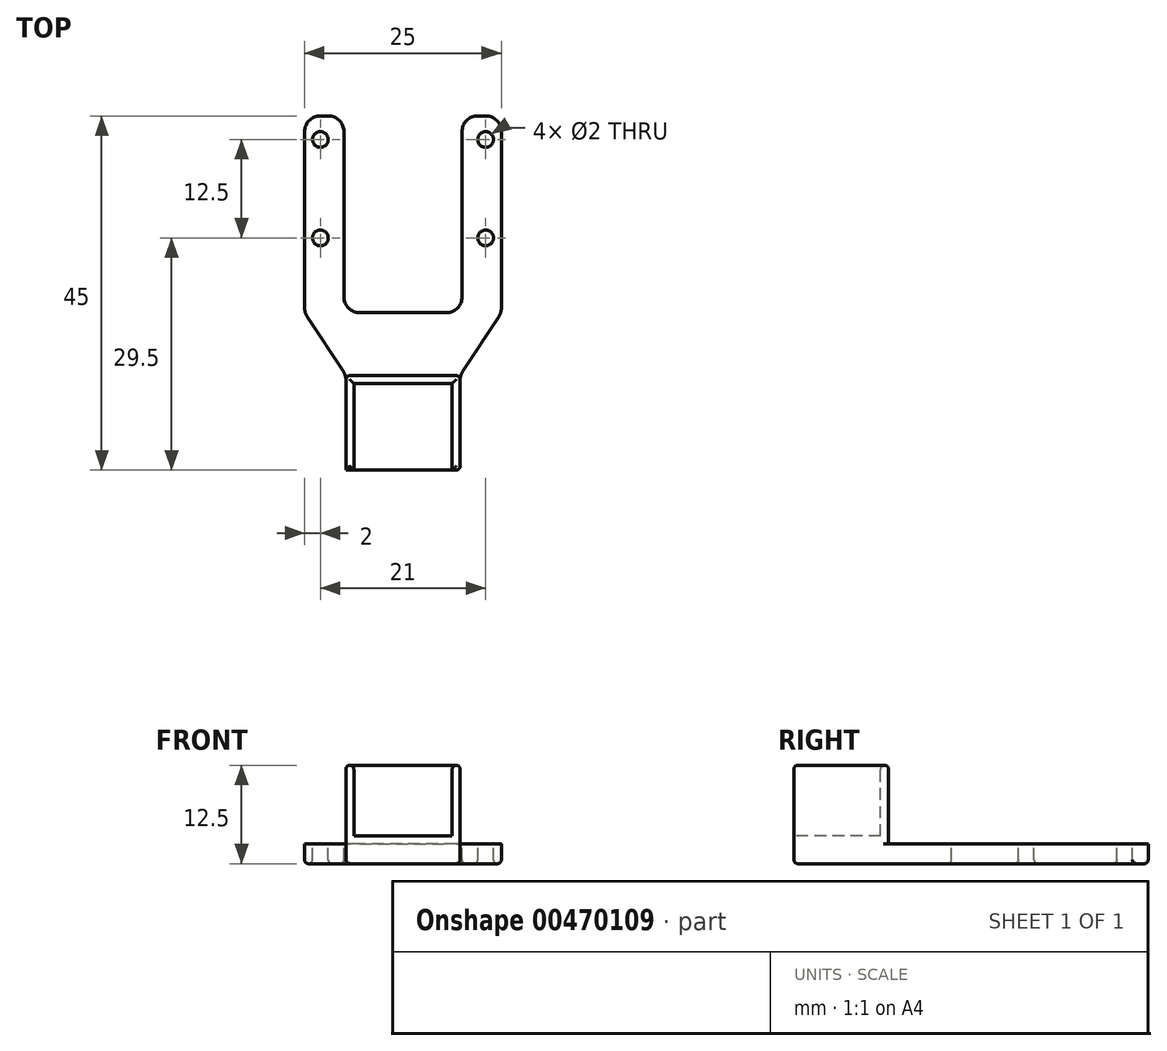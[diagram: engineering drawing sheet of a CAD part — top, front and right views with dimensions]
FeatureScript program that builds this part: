
annotation { "Feature Type Name" : "Feature", "Feature Type Description" : "" }
export const myFeature = defineFeature(function(context is Context, id is Id, definition is map)
    precondition{}
    {
        {
            var Q0;
            Q0=qCreatedBy(makeId("Top.planeOp"),FACE);
            var sketch = newSketch(context, id + "F0", { "sketchPlane" : qUnion([Q0])});
            skLineSegment(sketch, "E0", {"start": v(0, 0) * mm, "end": v(14.5, 0) * mm});
            skLineSegment(sketch, "E1", {"start": v(14.5, 0) * mm, "end": v(14.5, 12) * mm});
            skLineSegment(sketch, "E2", {"start": v(14.5, 12) * mm, "end": v(0, 12) * mm});
            skLineSegment(sketch, "E3", {"start": v(0, 12) * mm, "end": v(0, 0) * mm});
            skSolve(sketch);
        }
        {
            var Q0;
            Q0=makeQuery(id+"F0.imprint","IMPRINT",FACE,{"disambiguationData":[TD([[makeQuery(id+"F0.imprint","IMPRINT",EDGE,{"derivedFrom":sQuery(id+"F0.wireOp",EDGE,"E0")}),1.0]])]});
            extrude(context, id + "F1", {"entities" : qUnion([Q0]), "depth" : 10 * mm});
        }
        {
            var Q0;
            Q0=makeQuery(id+"F1.opExtrude","CAP_FACE",FACE,{"disambiguationData":[OSD([sQuery(id+"F0.wireOp",EDGE,"E0"),sQuery(id+"F0.wireOp",EDGE,"E1"),sQuery(id+"F0.wireOp",EDGE,"E2"),sQuery(id+"F0.wireOp",EDGE,"E3")])],"isStart":false});
            var sketch = newSketch(context, id + "F2", { "sketchPlane" : qUnion([Q0])});
            skLineSegment(sketch, "E4.0", {"start": v(1, 11) * mm, "end": v(1, 0) * mm});
            skLineSegment(sketch, "E4.1", {"start": v(13.5, 11) * mm, "end": v(1, 11) * mm});
            skLineSegment(sketch, "E4.2", {"start": v(13.5, 0) * mm, "end": v(13.5, 11) * mm});
            skLineSegment(sketch, "E5", {"start": v(1, 0) * mm, "end": v(13.5, 0) * mm});
            skSolve(sketch);
        }
        {
            var Q0;
            Q0 = qSketchRegion(id + "F2", true);
            extrude(context, id + "F3", {"entities" : qUnion([Q0]), "operationType" : NewBodyOperationType.REMOVE, "oppositeDirection" : true, "depth" : 9 * mm});
        }
        {
            var Q0;
            Q0=makeQuery(id+"F1.opExtrude","CAP_FACE",FACE,{"disambiguationData":[OSD([sQuery(id+"F0.wireOp",EDGE,"E0"),sQuery(id+"F0.wireOp",EDGE,"E1"),sQuery(id+"F0.wireOp",EDGE,"E2"),sQuery(id+"F0.wireOp",EDGE,"E3")])],"isStart":true});
            var sketch = newSketch(context, id + "F4", { "sketchPlane" : qUnion([Q0])});
            skLineSegment(sketch, "E6.bottom", {"start": v(2, 0) * mm, "end": v(12.5, 0) * mm});
            skLineSegment(sketch, "E6.top", {"start": v(1.75, -20) * mm, "end": v(12.75, -20) * mm});
            skLineSegment(sketch, "E6.left", {"start": v(0, 0) * mm, "end": v(0, -12) * mm});
            skLineSegment(sketch, "E6.right", {"start": v(14.5, -2) * mm, "end": v(14.5, -11.4) * mm});
            skLineSegment(sketch, "E7", {"start": v(7.25, -20) * mm, "end": v(7.25, -26.02) * mm, "construction": true});
            skLineSegment(sketch, "E8.0", {"start": v(19.75, -20.6) * mm, "end": v(19.75, -43) * mm});
            skLineSegment(sketch, "E9", {"start": v(14.5, -20) * mm, "end": v(14.75, -20) * mm});
            skLineSegment(sketch, "E10.0", {"start": v(14.75, -22) * mm, "end": v(14.75, -43) * mm});
            skLineSegment(sketch, "E11", {"start": v(17.75, -45) * mm, "end": v(16.75, -45) * mm});
            skLineSegment(sketch, "E12", {"start": v(19.42, -19.5) * mm, "end": v(14.83, -12.5) * mm});
            skLineSegment(sketch, "E13.MirrorCS", {"start": v(-0.25, -22) * mm, "end": v(-0.25, -43) * mm});
            skLineSegment(sketch, "E14.MirrorCS", {"start": v(-3.25, -45) * mm, "end": v(-2.25, -45) * mm});
            skLineSegment(sketch, "E15.MirrorCS", {"start": v(-5.25, -20.6) * mm, "end": v(-5.25, -43) * mm});
            skLineSegment(sketch, "E16.MirrorCS", {"start": v(-4.92, -19.5) * mm, "end": v(-0.33, -12.5) * mm});
            skLineSegment(sketch, "E17.MirrorCS", {"start": v(0, -20) * mm, "end": v(-0.25, -20) * mm});
            skPoint(sketch, "E18.orphan", {"position": v(-5.25, -20) * mm});
            skCircle(sketch, "E19", {"center": v(17.75, -42) * mm, "radius": 1 * mm});
            skCircle(sketch, "E20", {"center": v(17.75, -29.5) * mm, "radius": 1 * mm});
            skCircle(sketch, "E21.MirrorC", {"center": v(-3.25, -29.5) * mm, "radius": 1 * mm});
            skCircle(sketch, "E22.MirrorC", {"center": v(-3.25, -42) * mm, "radius": 1 * mm});
            skLineSegment(sketch, "E23.top", {"start": v(14.5, 0) * mm, "end": v(0, 0) * mm});
            skLineSegment(sketch, "E23.left", {"start": v(14.5, -12) * mm, "end": v(14.5, 0) * mm});
            skLineSegment(sketch, "E23.right", {"start": v(0, -11.4) * mm, "end": v(0, -2) * mm});
            skPoint(sketch, "E24.visualSharp", {"position": v(14.75, -45) * mm});
            skArc(sketch, "E24.filletArc", {"start": v(14.75, -43) * mm, "mid": v(15.34, -44.41) * mm, "end": v(16.75, -45) * mm});
            skPoint(sketch, "E25.visualSharp", {"position": v(19.75, -45) * mm});
            skArc(sketch, "E25.filletArc", {"start": v(17.75, -45) * mm, "mid": v(19.16, -44.41) * mm, "end": v(19.75, -43) * mm});
            skPoint(sketch, "E26.newPointA", {"position": v(14.75, -20) * mm});
            skPoint(sketch, "E26.newPointB", {"position": v(14.5, -20) * mm});
            skArc(sketch, "E26.filletArc", {"start": v(14.75, -22) * mm, "mid": v(14.16, -20.59) * mm, "end": v(12.75, -20) * mm});
            skPoint(sketch, "E27.newPointA", {"position": v(-0.25, -20) * mm});
            skPoint(sketch, "E27.newPointB", {"position": v(0, -20) * mm});
            skArc(sketch, "E27.filletArc", {"start": v(1.75, -20) * mm, "mid": v(0.34, -20.59) * mm, "end": v(-0.25, -22) * mm});
            skPoint(sketch, "E28.visualSharp", {"position": v(-0.25, -45) * mm});
            skArc(sketch, "E28.filletArc", {"start": v(-2.25, -45) * mm, "mid": v(-0.84, -44.41) * mm, "end": v(-0.25, -43) * mm});
            skPoint(sketch, "E29.visualSharp", {"position": v(-5.25, -45) * mm});
            skArc(sketch, "E29.filletArc", {"start": v(-5.25, -43) * mm, "mid": v(-4.66, -44.41) * mm, "end": v(-3.25, -45) * mm});
            skArc(sketch, "E30.filletArc", {"start": v(-4.92, -19.5) * mm, "mid": v(-5.17, -20.03) * mm, "end": v(-5.25, -20.6) * mm});
            skPoint(sketch, "E31.visualSharp", {"position": v(19.75, -20) * mm});
            skArc(sketch, "E31.filletArc", {"start": v(19.75, -20.6) * mm, "mid": v(19.67, -20.03) * mm, "end": v(19.42, -19.5) * mm});
            skPoint(sketch, "E32.visualSharp", {"position": v(14.5, 0) * mm});
            skArc(sketch, "E32.filletArc", {"start": v(14.5, -2) * mm, "mid": v(13.91, -0.59) * mm, "end": v(12.5, 0) * mm});
            skPoint(sketch, "E33.visualSharp", {"position": v(14.5, -12) * mm});
            skArc(sketch, "E33.filletArc", {"start": v(14.5, -11.4) * mm, "mid": v(14.58, -11.97) * mm, "end": v(14.83, -12.5) * mm});
            skPoint(sketch, "E34.visualSharp", {"position": v(0, -12) * mm});
            skArc(sketch, "E34.filletArc", {"start": v(-0.33, -12.5) * mm, "mid": v(-0.08, -11.97) * mm, "end": v(0, -11.4) * mm});
            skPoint(sketch, "E35.visualSharp", {"position": v(0, 0) * mm});
            skArc(sketch, "E35.filletArc", {"start": v(2, 0) * mm, "mid": v(0.59, -0.59) * mm, "end": v(0, -2) * mm});
            skSolve(sketch);
        }
        {
            var Q0;
            Q0 = qSketchRegion(id + "F4", true);
            extrude(context, id + "F5", {"entities" : qUnion([Q0]), "operationType" : NewBodyOperationType.ADD, "depth" : 2.5 * mm});
        }
        {
            var Q0;
            Q0=makeQuery(id+"F1.opExtrude","SWEPT_EDGE",EDGE,{"disambiguationData":[OSD([sQuery(id+"F0.wireOp",EDGE,"E1"),sQuery(id+"F0.wireOp",EDGE,"E2")])]});
            var Q1;
            Q1=makeQuery(id+"F1.opExtrude","SWEPT_EDGE",EDGE,{"disambiguationData":[OSD([sQuery(id+"F0.wireOp",EDGE,"E2"),sQuery(id+"F0.wireOp",EDGE,"E3")])]});
            var Q2;
            Q2=makeQuery(id+"F5.boolean.opBoolean","MERGE",EDGE,{"derivedFrom":[makeQuery(id+"F1.opExtrude","SWEPT_EDGE",EDGE,{"disambiguationData":[OSD([sQuery(id+"F0.wireOp",EDGE,"E0"),sQuery(id+"F0.wireOp",EDGE,"E1")])]}),makeQuery(id+"F5.opExtrude","SWEPT_EDGE",EDGE,{"disambiguationData":[OSD([sQuery(id+"F4.wireOp",EDGE,"E23.top"),sQuery(id+"F4.wireOp",EDGE,"E23.left")])]})]});
            var Q3;
            Q3=makeQuery(id+"F3.boolean.opBoolean","COPY",EDGE,{"derivedFrom":makeQuery(id+"F3.opExtrude","SWEPT_EDGE",EDGE,{"disambiguationData":[OSD([sQuery(id+"F0.wireOp",EDGE,"E0"),sQuery(id+"F2.wireOp",EDGE,"E4.0"),sQuery(id+"F2.wireOp",EDGE,"E5")])]})});
            var Q4;
            Q4=makeQuery(id+"F5.opExtrude","CAP_EDGE",EDGE,{"disambiguationData":[OSD([sQuery(id+"F4.wireOp",EDGE,"E23.left")])],"isStart":false});
            var Q5;
            Q5=makeQuery(id+"F5.opExtrude","CAP_FACE",FACE,{"disambiguationData":[OSD([sQuery(id+"F4.wireOp",EDGE,"E6.top"),sQuery(id+"F4.wireOp",EDGE,"E6.left"),sQuery(id+"F4.wireOp",EDGE,"E8.0"),sQuery(id+"F4.wireOp",EDGE,"E10.0"),sQuery(id+"F4.wireOp",EDGE,"E11"),sQuery(id+"F4.wireOp",EDGE,"E12"),sQuery(id+"F4.wireOp",EDGE,"E13.MirrorCS"),sQuery(id+"F4.wireOp",EDGE,"E14.MirrorCS"),sQuery(id+"F4.wireOp",EDGE,"E15.MirrorCS"),sQuery(id+"F4.wireOp",EDGE,"E16.MirrorCS"),sQuery(id+"F4.wireOp",EDGE,"E19"),sQuery(id+"F4.wireOp",EDGE,"E20"),sQuery(id+"F4.wireOp",EDGE,"E21.MirrorC"),sQuery(id+"F4.wireOp",EDGE,"E22.MirrorC"),sQuery(id+"F4.wireOp",EDGE,"E23.top"),sQuery(id+"F4.wireOp",EDGE,"E23.left"),sQuery(id+"F4.wireOp",EDGE,"E23.right"),sQuery(id+"F4.wireOp",EDGE,"E24.filletArc"),sQuery(id+"F4.wireOp",EDGE,"E25.filletArc"),sQuery(id+"F4.wireOp",EDGE,"E26.filletArc"),sQuery(id+"F4.wireOp",EDGE,"E27.filletArc"),sQuery(id+"F4.wireOp",EDGE,"E28.filletArc"),sQuery(id+"F4.wireOp",EDGE,"E29.filletArc"),sQuery(id+"F4.wireOp",EDGE,"E30.filletArc"),sQuery(id+"F4.wireOp",EDGE,"E31.filletArc"),sQuery(id+"F4.wireOp",EDGE,"E33.filletArc"),sQuery(id+"F4.wireOp",EDGE,"E34.filletArc")])],"isStart":false});
            var Q6;
            Q6=makeQuery(id+"F3.boolean.opBoolean","COPY",EDGE,{"derivedFrom":makeQuery(id+"F3.opExtrude","CAP_EDGE",EDGE,{"disambiguationData":[OSD([sQuery(id+"F2.wireOp",EDGE,"E5")])],"isStart":false})});
            var Q7;
            Q7=makeQuery(id+"F1.opExtrude","CAP_EDGE",EDGE,{"disambiguationData":[OSD([sQuery(id+"F0.wireOp",EDGE,"E3")])],"isStart":false});
            var Q8;
            Q8=makeQuery(id+"F3.boolean.opBoolean","COPY",EDGE,{"derivedFrom":makeQuery(id+"F3.opExtrude","CAP_EDGE",EDGE,{"disambiguationData":[OSD([sQuery(id+"F2.wireOp",EDGE,"E4.0")])],"isStart":true})});
            var Q9;
            Q9=makeQuery(id+"F3.boolean.opBoolean","COPY",EDGE,{"derivedFrom":makeQuery(id+"F3.opExtrude","CAP_EDGE",EDGE,{"disambiguationData":[OSD([sQuery(id+"F2.wireOp",EDGE,"E4.1")])],"isStart":true})});
            var Q10;
            Q10=makeQuery(id+"F1.opExtrude","CAP_FACE",FACE,{"disambiguationData":[OSD([sQuery(id+"F0.wireOp",EDGE,"E0"),sQuery(id+"F0.wireOp",EDGE,"E1"),sQuery(id+"F0.wireOp",EDGE,"E2"),sQuery(id+"F0.wireOp",EDGE,"E3")])],"isStart":false});
            fillet(context, id + "F6", {"entities" : qUnion([Q0, Q1, Q2, Q3, Q4, Q5, Q6, Q7, Q8, Q9, Q10]), "radius" : 0.5 * mm, "tangentPropagation" : true, "allowEdgeOverflow" : false});
        }
    });
